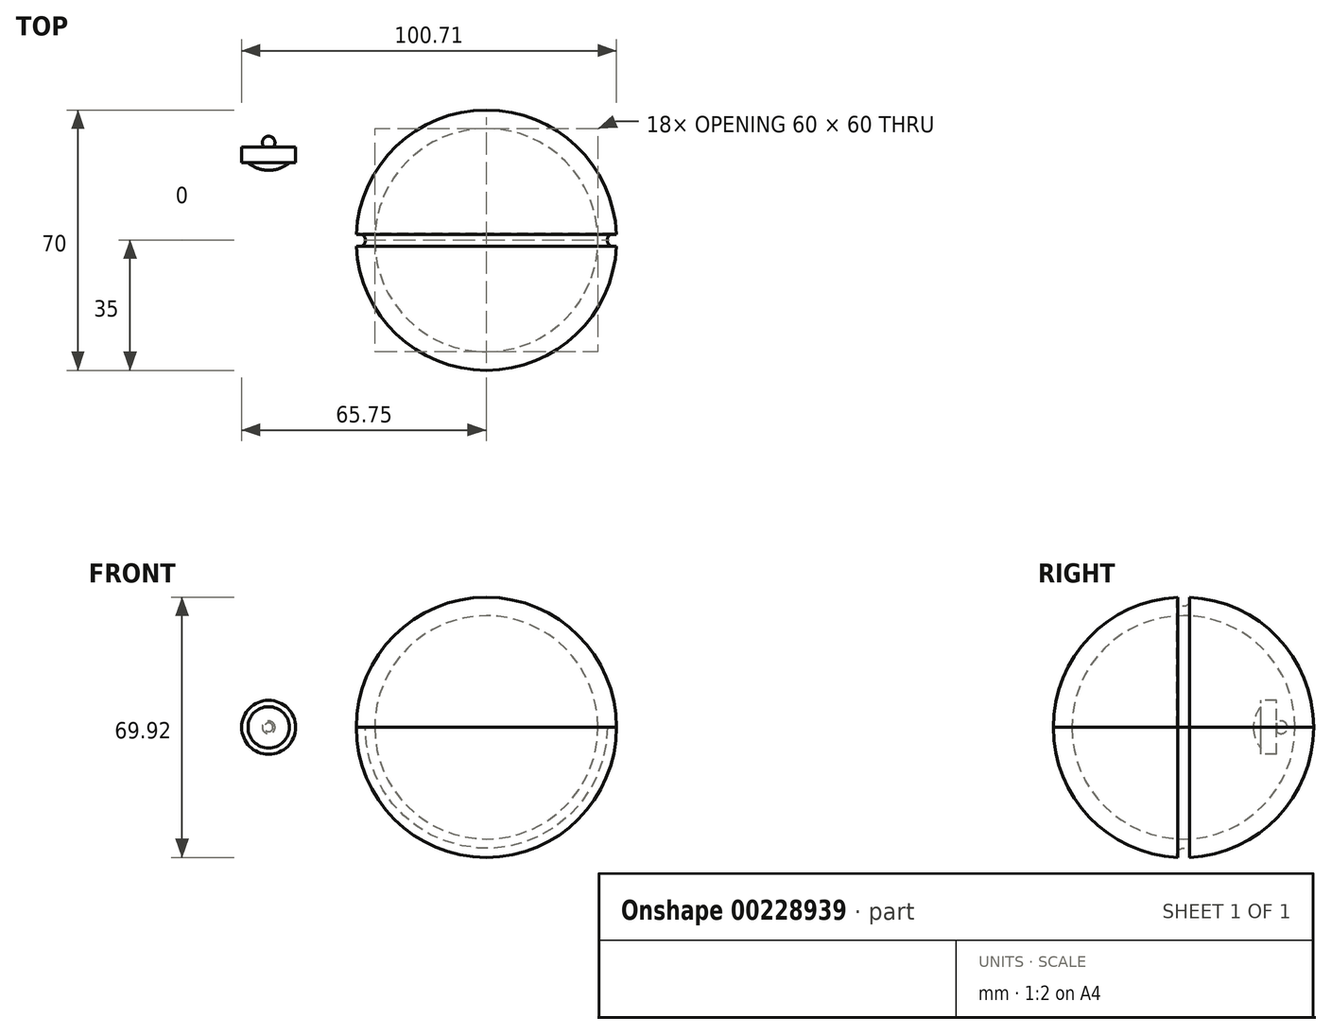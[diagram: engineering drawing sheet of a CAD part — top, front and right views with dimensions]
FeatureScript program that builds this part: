
annotation { "Feature Type Name" : "Feature", "Feature Type Description" : "" }
export const myFeature = defineFeature(function(context is Context, id is Id, definition is map)
    precondition{}
    {
        {
            var Q0;
            Q0=qCreatedBy(makeId("Top.planeOp"),FACE);
            var sketch = newSketch(context, id + "F0", { "sketchPlane" : qUnion([Q0])});
            skArc(sketch, "E0", {"start": v(0, 35) * mm, "mid": v(-35, 0) * mm, "end": v(0, -35) * mm});
            skArc(sketch, "E1", {"start": v(0, 30) * mm, "mid": v(-30, 0) * mm, "end": v(0, -30) * mm});
            skLineSegment(sketch, "E2", {"start": v(0, 35) * mm, "end": v(0, 30) * mm});
            skLineSegment(sketch, "E3", {"start": v(0, -30) * mm, "end": v(0, -35) * mm});
            skCircle(sketch, "E4", {"center": v(-34.25, 0) * mm, "radius": 1.75 * mm});
            skPoint(sketch, "E5", {"position": v(-35, 0) * mm});
            skSolve(sketch);
        }
        {
            var Q0;
            Q0=qCreatedBy(makeId("Top.planeOp"),FACE);
            var sketch = newSketch(context, id + "F1", { "sketchPlane" : qUnion([Q0])});
            skLineSegment(sketch, "E6", {"start": v(0, 35.31) * mm, "end": v(0, -35.2) * mm});
            skSolve(sketch);
        }
        {
            var Q0;
            Q0=makeQuery(id+"F0.imprint","IMPRINT",FACE,{"disambiguationData":[TD([[makeQuery(id+"F0.imprint","IMPRINT",EDGE,{"derivedFrom":sQuery(id+"F0.wireOp",EDGE,"E1")}),-1.0]])]});
            var Q1;
            Q1=sQuery(id+"F1.wireOp",EDGE,"E6");
            revolve(context, id + "F2", {"entities" : qUnion([Q0]), "axis" : qUnion([Q1]), "revolveType" : RevolveType.ONE_DIRECTION, "angle" : 180 * degree});
        }
        {
            var Q0;
            Q0=makeQuery(id+"F2.opRevolve","SWEPT_BODY",BODY,{"disambiguationData":[OSD([sQuery(id+"F0.wireOp",EDGE,"E0"),sQuery(id+"F0.wireOp",EDGE,"E1"),sQuery(id+"F0.wireOp",EDGE,"E2"),sQuery(id+"F0.wireOp",EDGE,"E3"),sQuery(id+"F0.wireOp",EDGE,"E4")])]});
            var Q1;
            Q1=qCreatedBy(makeId("Top.planeOp"),FACE);
            mirror(context, id + "F3", {"entities" : qUnion([Q0]), "mirrorPlane" : qUnion([Q1])});
        }
        {
            var Q0;
            Q0=qCreatedBy(makeId("Top.planeOp"),FACE);
            var sketch = newSketch(context, id + "F4", { "sketchPlane" : qUnion([Q0])});
            skCircle(sketch, "E7", {"center": v(-58.5, 26.23) * mm, "radius": 1.7 * mm});
            skLineSegment(sketch, "E8", {"start": v(-58.5, 27.93) * mm, "end": v(-58.5, 24.53) * mm});
            skSolve(sketch);
        }
        {
            var Q0;
            Q0=qCreatedBy(makeId("Front.planeOp"),FACE);
            var sketch = newSketch(context, id + "F5", { "sketchPlane" : qUnion([Q0])});
            skCircle(sketch, "E9", {"center": v(-58.5, 0) * mm, "radius": 7.25 * mm});
            skSolve(sketch);
        }
        {
            var Q0;
            Q0=makeQuery(id+"F5.imprint","IMPRINT",FACE,{"disambiguationData":[TD([[makeQuery(id+"F5.imprint","IMPRINT",EDGE,{"derivedFrom":sQuery(id+"F5.wireOp",EDGE,"E9")}),1.0]])]});
            extrude(context, id + "F6", {"entities" : qUnion([Q0]), "oppositeDirection" : true, "depth" : 25 * mm});
        }
        {
            var Q0;
            {var subQ0=sQuery(id+"F4.wireOp",EDGE,"E8");Q0=makeQuery(id+"F4.imprint","IMPRINT",FACE,{"disambiguationData":[TD([[makeQuery(id+"F4.imprint","IMPRINT",EDGE,{"derivedFrom":subQ0}),-1.0]])]});}
            var Q1;
            Q1=sQuery(id+"F4.wireOp",EDGE,"E8");
            revolve(context, id + "F7", {"operationType" : NewBodyOperationType.ADD, "entities" : qUnion([Q0]), "axis" : qUnion([Q1]), "revolveType" : RevolveType.FULL});
        }
        {
            var Q0;
            Q0=qCreatedBy(makeId("Front.planeOp"),FACE);
            var sketch = newSketch(context, id + "F8", { "sketchPlane" : qUnion([Q0])});
            skLineSegment(sketch, "E10.bottom", {"start": v(-69.13, 9.63) * mm, "end": v(-42.6, 9.63) * mm});
            skLineSegment(sketch, "E10.top", {"start": v(-69.13, -10.46) * mm, "end": v(-42.6, -10.46) * mm});
            skLineSegment(sketch, "E10.left", {"start": v(-69.13, 9.63) * mm, "end": v(-69.13, -10.46) * mm});
            skLineSegment(sketch, "E10.right", {"start": v(-42.6, 9.63) * mm, "end": v(-42.6, -10.46) * mm});
            skSolve(sketch);
        }
        {
            var Q0;
            Q0=makeQuery(id+"F8.imprint","IMPRINT",FACE,{"disambiguationData":[TD([[makeQuery(id+"F8.imprint","IMPRINT",EDGE,{"derivedFrom":sQuery(id+"F8.wireOp",EDGE,"E10.bottom")}),-1.0]])]});
            extrude(context, id + "F9", {"entities" : qUnion([Q0]), "operationType" : NewBodyOperationType.REMOVE, "oppositeDirection" : true, "depth" : 20.8 * mm});
        }
        {
            var Q0;
            Q0=makeQuery(id+"F9.boolean.opBoolean","COPY",FACE,{"derivedFrom":makeQuery(id+"F9.opExtrude","CAP_FACE",FACE,{"disambiguationData":[OSD([sQuery(id+"F8.wireOp",EDGE,"E10.bottom"),sQuery(id+"F8.wireOp",EDGE,"E10.top"),sQuery(id+"F8.wireOp",EDGE,"E10.left"),sQuery(id+"F8.wireOp",EDGE,"E10.right")])],"isStart":false})});
            var sketch = newSketch(context, id + "F10", { "sketchPlane" : qUnion([Q0])});
            skCircle(sketch, "E11", {"center": v(-58.5, 0) * mm, "radius": 5.55 * mm});
            skSolve(sketch);
        }
        {
            var Q0;
            Q0=makeQuery(id+"F10.imprint","IMPRINT",FACE,{"disambiguationData":[TD([[makeQuery(id+"F10.imprint","IMPRINT",EDGE,{"derivedFrom":sQuery(id+"F10.wireOp",EDGE,"E11")}),1.0]])]});
            extrude(context, id + "F11", {"entities" : qUnion([Q0]), "operationType" : NewBodyOperationType.ADD, "depth" : 2 * mm});
        }
        {
            var Q0;
            Q0=makeQuery(id+"F11.opExtrude","CAP_EDGE",EDGE,{"disambiguationData":[OSD([sQuery(id+"F10.wireOp",EDGE,"E11")])],"isStart":false});
            fillet(context, id + "F12", {"entities" : qUnion([Q0]), "radius" : 8.68 * mm, "tangentPropagation" : true, "allowEdgeOverflow" : false});
        }
    });
